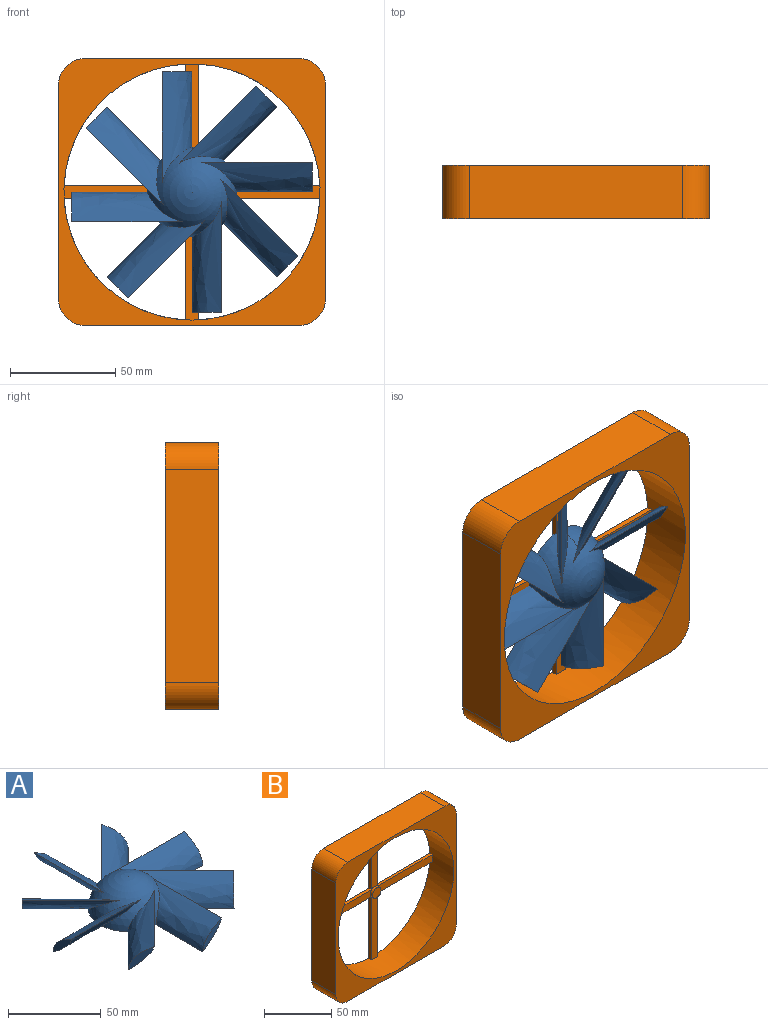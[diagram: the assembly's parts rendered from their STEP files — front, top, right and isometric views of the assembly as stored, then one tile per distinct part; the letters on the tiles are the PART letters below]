
ASSEMBLY  parts=2 mates=1
PART A: 29 faces, bbox 114.3x114.3x21.4 mm
  f0: extruded ~47.04x47.04mm, area 880.8mm2, adj f1,f2,f21
  f1: extruded ~47.04x47.04mm, area 854.1mm2, adj f0,f2,f21
  f2: plane 15.44x9.96mm, normal (0.71,-0.71,0), area 63.3mm2, adj f0,f1
  f3: extruded ~52.43x15.44mm, area 880.8mm2, adj f4,f5,f21
  f4: extruded ~52.43x15.44mm, area 854.1mm2, adj f3,f5,f21
  f5: plane 15.44x14.09mm, normal (0,-1,0), area 63.3mm2, adj f3,f4
  f6: extruded ~47.04x47.04mm, area 880.8mm2, adj f7,f8,f21
  f7: extruded ~47.04x47.04mm, area 854.1mm2, adj f6,f8,f21
  f8: plane 15.44x9.96mm, normal (-0.71,-0.71,0), area 63.3mm2, adj f6,f7
  f9: extruded ~52.43x15.44mm, area 880.8mm2, adj f10,f11,f21
  f10: extruded ~52.43x15.44mm, area 854.1mm2, adj f9,f11,f21
  f11: plane 15.44x14.09mm, normal (-1,0,0), area 63.3mm2, adj f9,f10
  f12: extruded ~47.04x47.04mm, area 880.8mm2, adj f13,f14,f21
  f13: extruded ~47.04x47.04mm, area 854.1mm2, adj f12,f14,f21
  f14: plane 15.44x9.96mm, normal (-0.71,0.71,0), area 63.3mm2, adj f12,f13
  f15: extruded ~52.43x15.44mm, area 880.8mm2, adj f16,f17,f21
  f16: extruded ~52.43x15.44mm, area 854.1mm2, adj f15,f17,f21
  f17: plane 15.44x14.09mm, normal (0,1,0), area 63.3mm2, adj f15,f16
  f18: extruded ~47.04x47.04mm, area 880.8mm2, adj f19,f20,f21
  f19: extruded ~47.04x47.04mm, area 854.1mm2, adj f18,f20,f21,f22
  f20: plane 15.44x9.96mm, normal (0.71,0.71,0), area 63.3mm2, adj f18,f19
  f21: sphere r=21.43mm, area 2147mm2, adj f0,f1,f3,f4,f6,f7,f9,f10
  f22: sphere r=21.43mm, area 104.2mm2, adj f19,f21,f23
  f23: plane 42.86x42.86mm, normal (0,0,-1), area 1284.4mm2, adj f21,f22,f24
  f24: cylinder r=7.1mm len=14.21mm, axis (0,0,-1), area 510.2mm2, adj f23,f25
  f25: plane 14.21x14.21mm, normal (0,0,-1), area 158.5mm2, adj f24
  f26: extruded ~52.43x15.44mm, area 880.8mm2, adj f21,f27,f28
  f27: extruded ~52.43x15.44mm, area 854.1mm2, adj f21,f26,f28
  f28: plane 15.44x14.09mm, normal (1,0,0), area 63.3mm2, adj f26,f27
PART B: 25 faces, bbox 127x25.4x127 mm
  f0: plane 57.79x6.35mm, normal (0,-1,0), area 361mm2, adj f3,f17,f18,f23
  f1: plane 57.79x6.35mm, normal (0,-1,0), area 361mm2, adj f3,f15,f16,f23
  f2: plane 57.79x6.35mm, normal (0,-1,0), area 361mm2, adj f3,f14,f21,f23
  f3: cylinder r=60.96mm len=121.92mm, axis (0,1,0), area 9664.2mm2, adj f0,f1,f2,f8,f9,f14,f15,f16
  f4: plane 101.6x25.4mm, normal (0,0,1), area 2580.6mm2, adj f8,f9,f10,f13
  f5: plane 101.6x25.4mm, normal (-1,0,0), area 2580.6mm2, adj f8,f9,f10,f11
  f6: plane 101.6x25.4mm, normal (0,0,-1), area 2580.6mm2, adj f8,f9,f11,f12
  f7: plane 101.6x25.4mm, normal (1,0,0), area 2580.6mm2, adj f8,f9,f12,f13
  f8: plane 127x127mm, normal (0,-1,0), area 4316mm2, adj f3,f4,f5,f6,f7,f10,f11,f12
  f9: plane 127x127mm, normal (0,1,0), area 5823.4mm2, adj f3,f4,f5,f6,f7,f10,f11,f12
  f10: cylinder r=12.7mm len=25.4mm, axis (0,-1,0), area 506.7mm2, adj f4,f5,f8,f9
  f11: cylinder r=12.7mm len=25.4mm, axis (0,1,0), area 506.7mm2, adj f5,f6,f8,f9
  f12: cylinder r=12.7mm len=25.4mm, axis (0,-1,0), area 506.7mm2, adj f6,f7,f8,f9
  f13: cylinder r=12.7mm len=25.4mm, axis (0,1,0), area 506.7mm2, adj f4,f7,f8,f9
  f14: plane 57.7x2.54mm, normal (0,0,1), area 146.6mm2, adj f2,f3,f9,f15
  f15: plane 57.7x2.54mm, normal (-1,0,0), area 146.6mm2, adj f1,f3,f9,f14
  f16: plane 57.7x2.54mm, normal (1,0,0), area 146.6mm2, adj f1,f3,f9,f17
  f17: plane 57.7x2.54mm, normal (0,0,1), area 146.6mm2, adj f0,f3,f9,f16
  f18: plane 57.7x2.54mm, normal (0,0,-1), area 146.6mm2, adj f0,f3,f9,f19
  f19: plane 57.7x2.54mm, normal (1,0,0), area 146.6mm2, adj f3,f9,f18,f22
  f20: plane 57.7x2.54mm, normal (-1,0,0), area 146.6mm2, adj f3,f9,f21,f22
  f21: plane 57.7x2.54mm, normal (0,0,-1), area 146.6mm2, adj f2,f3,f9,f20
  f22: plane 57.79x6.35mm, normal (0,-1,0), area 361mm2, adj f3,f19,f20,f23
  f23: cylinder r=4.49mm len=8.98mm, axis (0,1,0), area 71.7mm2, adj f0,f1,f2,f22,f24
  f24: plane 8.98x8.98mm, normal (0,-1,0), area 63.3mm2, adj f23
PLACE A rot(axis=(1,0,0),90deg) t=(-0.36,9.72,-0.35)mm
PLACE B t=(-0.36,11.62,-0.35)mm
MATE revolute A.f24 <-> B.f23  axis (0,1,0) through (-0.36,4,-0.35)mm
